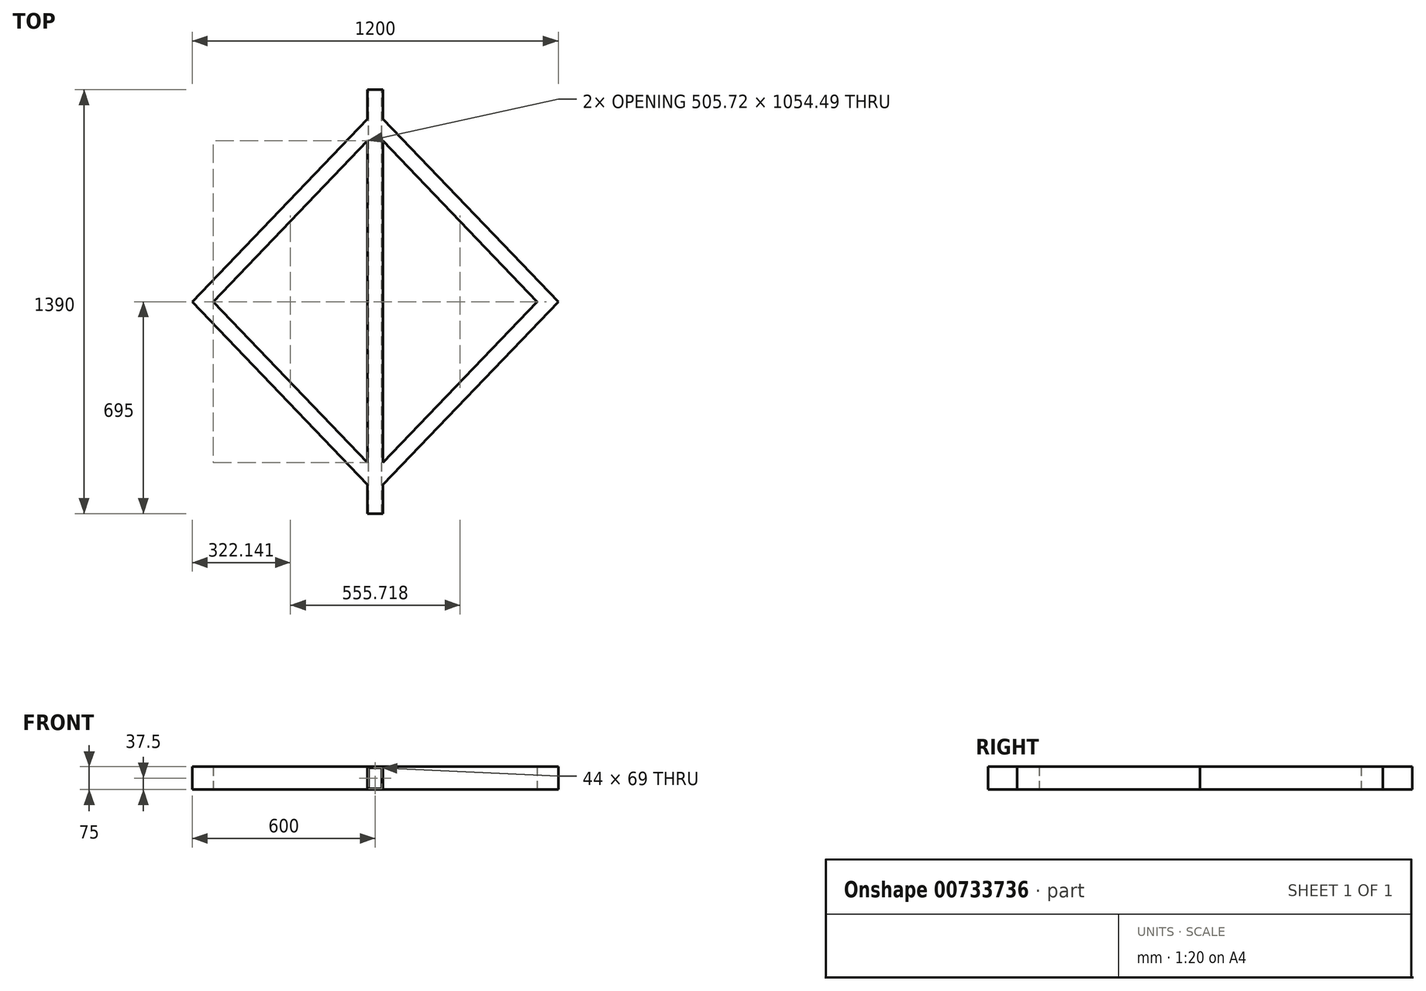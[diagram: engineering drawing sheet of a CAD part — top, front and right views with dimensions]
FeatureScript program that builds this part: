
annotation { "Feature Type Name" : "Feature", "Feature Type Description" : "" }
export const myFeature = defineFeature(function(context is Context, id is Id, definition is map)
    precondition{}
    {
        {
            var Q0;
            Q0=qCreatedBy(makeId("Front.planeOp"),FACE);
            var sketch = newSketch(context, id + "F0", { "sketchPlane" : qUnion([Q0])});
            skLineSegment(sketch, "E0.bottom", {"start": v(25, -37.5) * mm, "end": v(-25, -37.5) * mm});
            skLineSegment(sketch, "E0.top", {"start": v(25, 37.5) * mm, "end": v(-25, 37.5) * mm});
            skLineSegment(sketch, "E0.left", {"start": v(25, -37.5) * mm, "end": v(25, 37.5) * mm});
            skLineSegment(sketch, "E0.right", {"start": v(-25, -37.5) * mm, "end": v(-25, 37.5) * mm});
            skPoint(sketch, "E0.middle", {"position": v(0, 0) * mm});
            skLineSegment(sketch, "E1.0", {"start": v(22, -34.5) * mm, "end": v(22, 34.5) * mm});
            skLineSegment(sketch, "E1.1", {"start": v(22, -34.5) * mm, "end": v(-22, -34.5) * mm});
            skLineSegment(sketch, "E1.2", {"start": v(-22, -34.5) * mm, "end": v(-22, 34.5) * mm});
            skLineSegment(sketch, "E1.3", {"start": v(22, 34.5) * mm, "end": v(-22, 34.5) * mm});
            skSolve(sketch);
        }
        {
            var Q0;
            Q0=makeQuery(id+"F0.imprint","IMPRINT",FACE,{"disambiguationData":[TD([[makeQuery(id+"F0.imprint","IMPRINT",EDGE,{"derivedFrom":sQuery(id+"F0.wireOp",EDGE,"E0.bottom")}),-1.0]])]});
            extrude(context, id + "F1", {"entities" : qUnion([Q0]), "endBound" : BoundingType.SYMMETRIC, "depth" : 1390 * mm, "offsetDistance" : 25 * mm});
        }
        {
            var Q0;
            Q0=makeQuery(id+"F1.opExtrude","SWEPT_FACE",FACE,{"disambiguationData":[OSD([sQuery(id+"F0.wireOp",EDGE,"E0.bottom")])]});
            var sketch = newSketch(context, id + "F2", { "sketchPlane" : qUnion([Q0])});
            skCircle(sketch, "E2", {"center": v(0, 0) * mm, "radius": 600 * mm});
            skLineSegment(sketch, "E3", {"start": v(0, 0) * mm, "end": v(600, 0) * mm});
            skLineSegment(sketch, "E4", {"start": v(600, 0) * mm, "end": v(25, 599.48) * mm});
            skLineSegment(sketch, "E5.0", {"start": v(530.72, 0) * mm, "end": v(25, 527.25) * mm});
            skLineSegment(sketch, "E6", {"start": v(25, 527.25) * mm, "end": v(25, 599.48) * mm});
            skSolve(sketch);
        }
        {
            var Q0;
            {var subQ0=sQuery(id+"F2.wireOp",EDGE,"E4");Q0=makeQuery(id+"F2.imprint","IMPRINT",FACE,{"disambiguationData":[TD([[makeQuery(id+"F2.imprint","IMPRINT",EDGE,{"derivedFrom":subQ0}),1.0]])]});}
            extrude(context, id + "F3", {"entities" : qUnion([Q0]), "operationType" : NewBodyOperationType.ADD, "oppositeDirection" : true, "depth" : 75 * mm, "offsetDistance" : 25 * mm});
        }
        {
            var Q0;
            Q0=makeQuery(id+"F1.opExtrude","SWEPT_BODY",BODY,{"disambiguationData":[OSD([sQuery(id+"F0.wireOp",EDGE,"E0.bottom"),sQuery(id+"F0.wireOp",EDGE,"E0.top"),sQuery(id+"F0.wireOp",EDGE,"E0.left"),sQuery(id+"F0.wireOp",EDGE,"E0.right"),sQuery(id+"F0.wireOp",EDGE,"E1.0"),sQuery(id+"F0.wireOp",EDGE,"E1.1"),sQuery(id+"F0.wireOp",EDGE,"E1.2"),sQuery(id+"F0.wireOp",EDGE,"E1.3")])]});
            var Q1;
            Q1=qCreatedBy(makeId("Right.planeOp"),FACE);
            mirror(context, id + "F4", {"operationType" : NewBodyOperationType.ADD, "entities" : qUnion([Q0]), "mirrorPlane" : qUnion([Q1])});
        }
        {
            var Q0;
            Q0=makeQuery(id+"F1.opExtrude","SWEPT_BODY",BODY,{"disambiguationData":[OSD([sQuery(id+"F0.wireOp",EDGE,"E0.bottom"),sQuery(id+"F0.wireOp",EDGE,"E0.top"),sQuery(id+"F0.wireOp",EDGE,"E0.left"),sQuery(id+"F0.wireOp",EDGE,"E0.right"),sQuery(id+"F0.wireOp",EDGE,"E1.0"),sQuery(id+"F0.wireOp",EDGE,"E1.1"),sQuery(id+"F0.wireOp",EDGE,"E1.2"),sQuery(id+"F0.wireOp",EDGE,"E1.3")])]});
            var Q1;
            Q1=qCreatedBy(makeId("Front.planeOp"),FACE);
            mirror(context, id + "F5", {"operationType" : NewBodyOperationType.ADD, "entities" : qUnion([Q0]), "mirrorPlane" : qUnion([Q1])});
        }
    });
